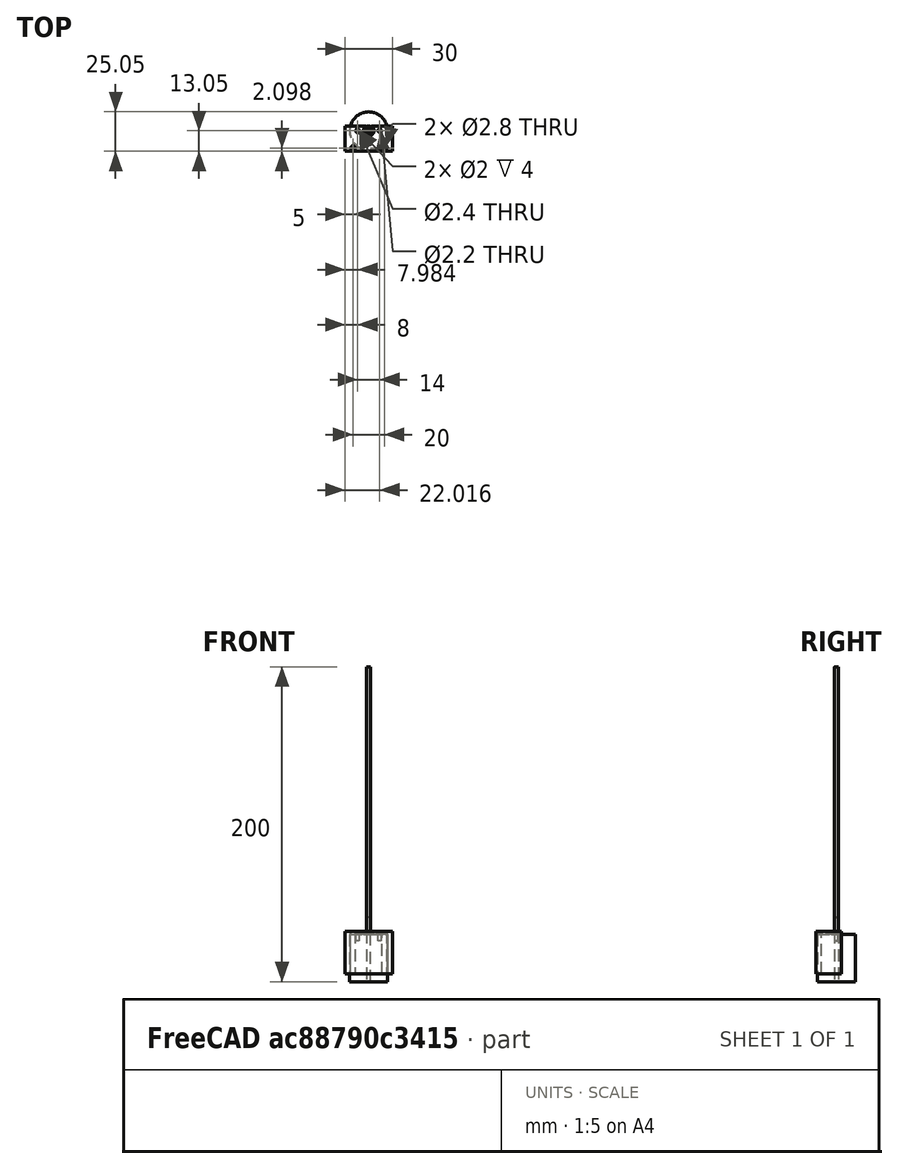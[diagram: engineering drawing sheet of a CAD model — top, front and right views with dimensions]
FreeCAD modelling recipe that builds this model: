
FCSTD DOCUMENT  (FreeCAD 0.19R24366 (Git))
Label: motor
License: All rights reserved
LicenseURL: http://en.wikipedia.org/wiki/All_rights_reserved
objects: Sketcher::SketchObject×10, PartDesign::Pad×6, PartDesign::Pocket×5, PartDesign::Body×3, App::Part×3, Mesh::Feature×1
note: 35 computed .brp shape members not serialized (recipe doc carries the construction recipe); baked Part::Feature solids carry a one-line shape summary decoded from their .brp

FEATURE [Sketcher::SketchObject] Sketch
  FullyConstrained = false
  MapMode = 5
  Support = -> [XY_Plane001]
  sketch-geometry (1):
    g0: Circle CenterX=0 CenterY=0 CenterZ=0 NormalX=0 NormalY=0 NormalZ=1 AngleXU=0 Radius=12
  constraints (1):
    c: Radius(g0) = 12
FEATURE [PartDesign::Pad] Pad  label="MotorMain"
  Direction = (1,1,1)
  Length = 30
  Length2 = 100
  Profile = -> Sketch
  Type = 0
FEATURE [Sketcher::SketchObject] Sketch001
  FullyConstrained = true
  MapMode = 5
  Placement = pos=(0,0,30) rot=(0,0,1;0rad)
  Support = -> [Pad]
  sketch-geometry (1):
    g0: Circle CenterX=0 CenterY=0 CenterZ=0 NormalX=0 NormalY=0 NormalZ=1 AngleXU=0 Radius=3
  constraints (2):
    c: Coincident(g0,g-1)
    c: Radius(g0) = 3
FEATURE [PartDesign::Pad] Pad001  label="MotorHeader"
  BaseFeature = -> Pad
  Direction = (1,1,1)
  Length = 1
  Length2 = 100
  Profile = -> Sketch001
  Type = 0
FEATURE [Sketcher::SketchObject] Sketch002
  FullyConstrained = true
  MapMode = 5
  Placement = pos=(0,0,31) rot=(0,0,1;0rad)
  Support = -> [Pad001]
  sketch-geometry (1):
    g0: Circle CenterX=0 CenterY=0 CenterZ=0 NormalX=0 NormalY=0 NormalZ=1 AngleXU=0 Radius=1
  constraints (2):
    c: Coincident(g0,g-1)
    c: Radius(g0) = 1
FEATURE [PartDesign::Pad] Pad002  label="Shaft"
  BaseFeature = -> Pad001
  Direction = (1,1,1)
  Length = 10
  Length2 = 100
  Profile = -> Sketch002
  Type = 0
FEATURE [Sketcher::SketchObject] Sketch003
  FullyConstrained = true
  MapMode = 5
  Placement = pos=(0,0,30) rot=(0,0,1;0rad)
  Support = -> [Pad002]
  sketch-geometry (4):
    g0: Circle CenterX=-7 CenterY=0 CenterZ=0 NormalX=0 NormalY=0 NormalZ=1 AngleXU=0 Radius=1
    g1: Circle CenterX=7 CenterY=0 CenterZ=0 NormalX=0 NormalY=0 NormalZ=1 AngleXU=0 Radius=1
    g2: LineSegment StartX=-7 StartY=0 StartZ=0 EndX=0 EndY=0 EndZ=0
    g3: LineSegment StartX=0 StartY=0 StartZ=0 EndX=7 EndY=0 EndZ=0
  constraints (10):
    c: PointOnObject(g0,g-1)
    c: PointOnObject(g1,g-1)
    c: Diameter(g1) = 2
    c: Diameter(g0) = 2
    c: Coincident(g2,g0)
    c: Coincident(g2,g-1)
    c: Coincident(g3,g2)
    c: Coincident(g3,g1)
    c: Equal(g3,g2)
    c: DistanceX(g2,g2) = 7
FEATURE [PartDesign::Pocket] Pocket
  BaseFeature = -> Pad002
  Length = 4
  Length2 = 100
  Profile = -> Sketch003
  Type = 0
FEATURE [PartDesign::Body] Body  label="MotorBody"
  Group = -> [Sketch,Pad,Sketch001,Pad001,Sketch002,Pad002,Sketch003,Pocket]
  Origin = -> Origin001
  Tip = -> Pocket
FEATURE [App::Part] Part  label="MotorPart"
  Group = -> [Body]
  Origin = -> Origin
FEATURE [Sketcher::SketchObject] Sketch004
  FullyConstrained = false
  Placement = pos=(0,0,30) rot=(0,0,1;0rad)
  sketch-geometry (6):
    g0: LineSegment StartX=-15 StartY=2.95461 StartZ=0 EndX=15 EndY=2.95461 EndZ=0
    g1: LineSegment StartX=15 StartY=2.95461 StartZ=0 EndX=15 EndY=-13.0454 EndZ=0
    g2: LineSegment StartX=15 StartY=-13.0454 StartZ=0 EndX=-15 EndY=-13.0454 EndZ=0
    g3: LineSegment StartX=-15 StartY=-13.0454 StartZ=0 EndX=-15 EndY=2.95461 EndZ=0
    g4: LineSegment StartX=-15 StartY=0 StartZ=0 EndX=0 EndY=0 EndZ=0
    g5: LineSegment StartX=0 StartY=0 StartZ=0 EndX=15 EndY=0 EndZ=0
  constraints (17):
    c: Coincident(g0,g1)
    c: Coincident(g1,g2)
    c: Coincident(g2,g3)
    c: Coincident(g3,g0)
    c: Horizontal(g0)
    c: Horizontal(g2)
    c: Vertical(g1)
    c: Vertical(g3)
    c: DistanceY(g1,g1) = 16
    c: DistanceX(g0,g0) = 30
    c: PointOnObject(g4,g3)
    c: Coincident(g4,g-1)
    c: Horizontal(g4)
    c: PointOnObject(g5,g1)
    c: Horizontal(g5)
    c: Equal(g4,g5)
    c: Coincident(g5,g-1)
FEATURE [PartDesign::Pad] Pad003
  Direction = (1,1,1)
  Length = 2
  Length2 = 100
  Placement = pos=(0,0,30) rot=(0,0,1;0rad)
  Profile = -> Sketch004
  Type = 0
FEATURE [Sketcher::SketchObject] Sketch005
  FullyConstrained = true
  MapMode = 5
  Placement = pos=(0,0,30) rot=(0,0,1;0rad)
  Support = -> [Pad]
  sketch-geometry (1):
    g0: Circle CenterX=0 CenterY=0 CenterZ=0 NormalX=0 NormalY=0 NormalZ=1 AngleXU=0 Radius=3.4
  constraints (2):
    c: Coincident(g0,g-1)
    c: Radius(g0) = 3.4
FEATURE [PartDesign::Pocket] Pocket001
  BaseFeature = -> Pad003
  Length = 20
  Length2 = 100
  Placement = pos=(0,0,30) rot=(0,0,1;0rad)
  Profile = -> Sketch005
  Reversed = true
  Type = 0
FEATURE [PartDesign::Pad] Pad004
  BaseFeature = -> Pocket001
  Direction = (1,1,1)
  Length = 25
  Length2 = 100
  Placement = pos=(0,0,30) rot=(0,0,1;0rad)
  Profile = -> Sketch004
  Reversed = true
  Type = 0
FEATURE [Sketcher::SketchObject] Sketch006
  FullyConstrained = false
  MapMode = 5
  Support = -> [XY_Plane003]
  sketch-geometry (1):
    g0: Circle CenterX=0 CenterY=0 CenterZ=0 NormalX=0 NormalY=0 NormalZ=1 AngleXU=0 Radius=12.2
  constraints (1):
    c: Radius(g0) = 12.2
FEATURE [PartDesign::Pocket] Pocket002
  BaseFeature = -> Pad004
  Length = 30
  Length2 = 100
  Placement = pos=(0,0,30) rot=(0,0,1;0rad)
  Profile = -> Sketch006
  Reversed = true
  Type = 0
FEATURE [Sketcher::SketchObject] Sketch007
  FullyConstrained = false
  MapMode = 5
  Placement = pos=(0,0,32) rot=(0,0,1;0rad)
  Support = -> [Pocket002]
  sketch-geometry (4):
    g0: Circle CenterX=-7.01627 CenterY=0 CenterZ=0 NormalX=0 NormalY=0 NormalZ=1 AngleXU=0 Radius=1.2
    g1: Circle CenterX=7.01627 CenterY=0 CenterZ=0 NormalX=0 NormalY=0 NormalZ=1 AngleXU=0 Radius=1.1
    g2: LineSegment StartX=-7.01627 StartY=0 StartZ=0 EndX=0 EndY=0 EndZ=0
    g3: LineSegment StartX=0 StartY=0 StartZ=0 EndX=7.01627 EndY=0 EndZ=0
  constraints (9):
    c: PointOnObject(g0,g-1)
    c: PointOnObject(g1,g-1)
    c: Diameter(g1) = 2.2
    c: Diameter(g0) = 2.4
    c: Coincident(g2,g0)
    c: Coincident(g2,g-1)
    c: Coincident(g3,g2)
    c: Coincident(g3,g1)
    c: Equal(g3,g2)
FEATURE [PartDesign::Pocket] Pocket003
  BaseFeature = -> Pocket002
  Length = 5
  Length2 = 100
  Placement = pos=(0,0,30) rot=(0,0,1;0rad)
  Profile = -> Sketch007
  Type = 0
FEATURE [Sketcher::SketchObject] Sketch008
  FullyConstrained = false
  MapMode = 5
  Placement = pos=(0,0,32) rot=(0,0,1;0rad)
  Support = -> [Pocket003]
  sketch-geometry (4):
    g0: Circle CenterX=-10 CenterY=-10.9518 CenterZ=0 NormalX=0 NormalY=0 NormalZ=1 AngleXU=0 Radius=1.4
    g1: Circle CenterX=10 CenterY=-10.9518 CenterZ=0 NormalX=0 NormalY=0 NormalZ=1 AngleXU=0 Radius=1.4
    g2: LineSegment StartX=10 StartY=-10.9518 StartZ=0 EndX=0 EndY=-10.9518 EndZ=0
    g3: LineSegment StartX=-10 StartY=-10.9518 StartZ=0 EndX=0 EndY=-10.9518 EndZ=0
  constraints (10):
    c: Horizontal(g1,g0)
    c: Coincident(g2,g1)
    c: PointOnObject(g2,g-2)
    c: Horizontal(g2)
    c: Coincident(g3,g0)
    c: Coincident(g3,g2)
    c: Equal(g2,g3)
    c: DistanceX(g0,g1) = 20
    c: Equal(g0,g1)
    c: Diameter(g0) = 2.8
FEATURE [PartDesign::Pocket] Pocket004
  BaseFeature = -> Pocket003
  Length = 50
  Length2 = 100
  Placement = pos=(0,0,30) rot=(0,0,1;0rad)
  Profile = -> Sketch008
  Type = 0
FEATURE [PartDesign::Body] Body001  label="MotorHolderBody"
  Group = -> [Sketch004,Pad003,Sketch005,Pocket001,Pad004,Sketch006,Pocket002,Sketch007,Pocket003,Sketch008,Pocket004]
  Origin = -> Origin003
  Tip = -> Pocket004
FEATURE [App::Part] Part001  label="MotorHolder"
  Group = -> [Body001]
  Origin = -> Origin002
FEATURE [Mesh::Feature] Mesh  label="MotorHolder (Meshed)"
FEATURE [Sketcher::SketchObject] Sketch013
  FullyConstrained = true
  MapMode = 5
  Support = -> [XY_Plane012]
  sketch-geometry (1):
    g0: Circle CenterX=0 CenterY=0 CenterZ=0 NormalX=0 NormalY=0 NormalZ=1 AngleXU=0 Radius=1.25
  constraints (2):
    c: Coincident(g0,g-1)
    c: Diameter(g0) = 2.5
FEATURE [PartDesign::Pad] Pad006
  Direction = (1,1,1)
  Length = 200
  Length2 = 100
  Profile = -> Sketch013
  Type = 0
FEATURE [PartDesign::Body] Body006
  Group = -> [Sketch013,Pad006]
  Origin = -> Origin012
  Tip = -> Pad006
FEATURE [App::Part] Part006  label="ConnectorRod2.5x200mm001"
  Group = -> [Body006]
  Origin = -> Origin013
